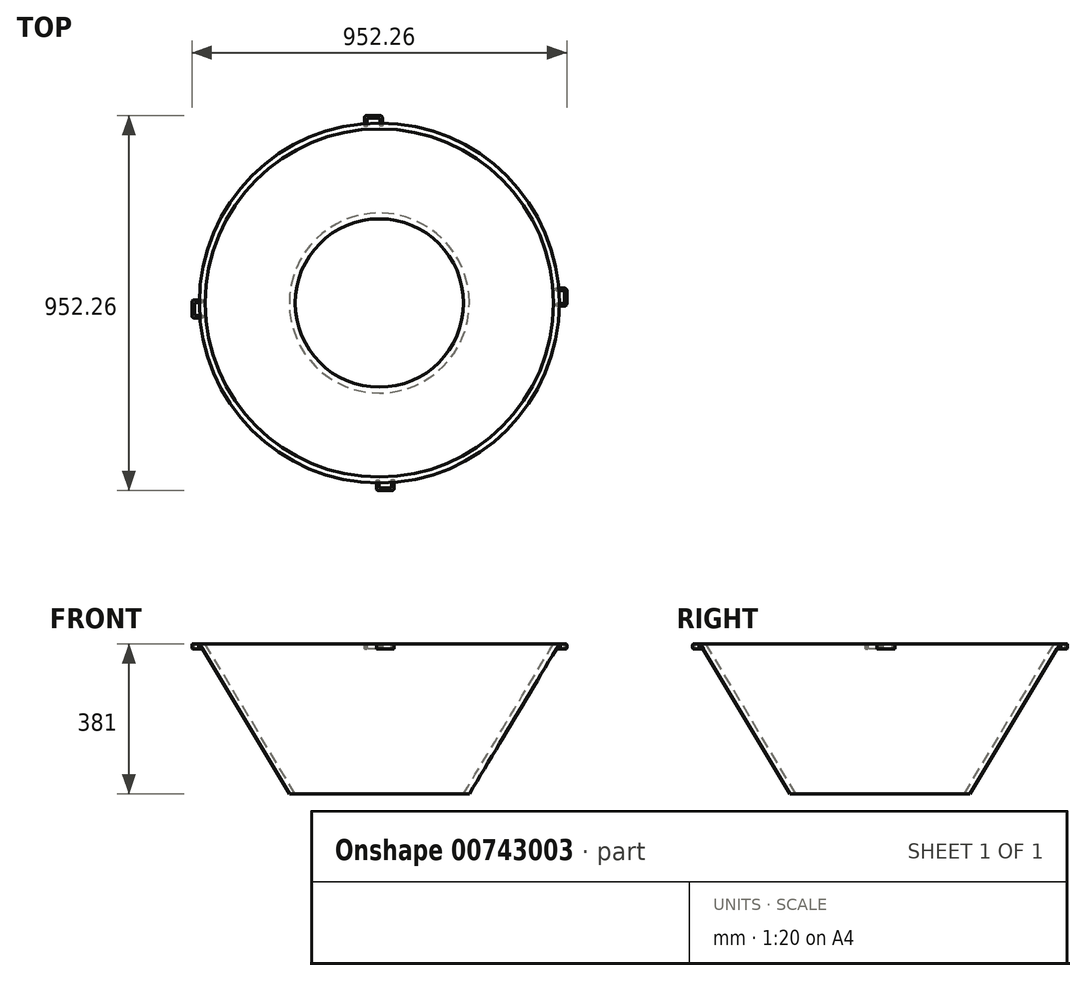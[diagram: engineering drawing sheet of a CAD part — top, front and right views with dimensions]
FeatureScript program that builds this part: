
annotation { "Feature Type Name" : "Feature", "Feature Type Description" : "" }
export const myFeature = defineFeature(function(context is Context, id is Id, definition is map)
    precondition{}
    {
        {
            var Q0;
            Q0=qCreatedBy(makeId("Top.planeOp"),FACE);
            var sketch = newSketch(context, id + "F0", { "sketchPlane" : qUnion([Q0])});
            skCircle(sketch, "E0", {"center": v(0, 0) * mm, "radius": 228.6 * mm});
            skSolve(sketch);
        }
        {
            var Q0;
            Q0=makeQuery(id+"F0.imprint","IMPRINT",FACE,{"disambiguationData":[TD([[makeQuery(id+"F0.imprint","IMPRINT",EDGE,{"derivedFrom":sQuery(id+"F0.wireOp",EDGE,"E0")}),1.0]])]});
            cPlane(context, id + "F1", {"entities" : qUnion([Q0]), "cplaneType" : CPlaneType.OFFSET, "offset" : 381 * mm, "width" : 152.4 * mm, "height" : 152.4 * mm});
        }
        {
            var Q0;
            Q0=qCreatedBy(id+"F1.planeOp",FACE);
            var sketch = newSketch(context, id + "F2", { "sketchPlane" : qUnion([Q0])});
            skCircle(sketch, "E1", {"center": v(0, 0) * mm, "radius": 457.2 * mm});
            skSolve(sketch);
        }
        {
            var Q0;
            Q0=makeQuery(id+"F0.imprint","IMPRINT",FACE,{"disambiguationData":[TD([[makeQuery(id+"F0.imprint","IMPRINT",EDGE,{"derivedFrom":sQuery(id+"F0.wireOp",EDGE,"E0")}),1.0]])]});
            var Q1;
            Q1=makeQuery(id+"F2.imprint","IMPRINT",FACE,{"disambiguationData":[TD([[makeQuery(id+"F2.imprint","IMPRINT",EDGE,{"derivedFrom":sQuery(id+"F2.wireOp",EDGE,"E1")}),1.0]])]});
            loft(context, id + "F3", {"sheetProfilesArray" : [{ "sheetProfileEntities" : qUnion([Q0]) }, { "sheetProfileEntities" : qUnion([Q1]) }]});
        }
        {
            var Q0;
            Q0=makeQuery(id+"F3.opLoft","CAP_FACE",FACE,{"disambiguationData":[OSD([makeQuery(id+"F2.imprint","IMPRINT",FACE,{"disambiguationData":[TD([[makeQuery(id+"F2.imprint","IMPRINT",EDGE,{"derivedFrom":sQuery(id+"F2.wireOp",EDGE,"E1")}),1.0]])]})])],"isStart":true});
            var Q1;
            Q1=makeQuery(id+"F3.opLoft","CAP_FACE",FACE,{"disambiguationData":[OSD([makeQuery(id+"F0.imprint","IMPRINT",FACE,{"disambiguationData":[TD([[makeQuery(id+"F0.imprint","IMPRINT",EDGE,{"derivedFrom":sQuery(id+"F0.wireOp",EDGE,"E0")}),1.0]])]})])],"isStart":true});
            shell(context, id + "F4", {"entities" : qUnion([Q0, Q1]), "thickness" : 12.7 * mm});
        }
        {
            var Q0;
            Q0=makeQuery(id+"F3.opLoft","CAP_FACE",FACE,{"disambiguationData":[OSD([makeQuery(id+"F2.imprint","IMPRINT",FACE,{"disambiguationData":[TD([[makeQuery(id+"F2.imprint","IMPRINT",EDGE,{"derivedFrom":sQuery(id+"F2.wireOp",EDGE,"E1")}),1.0]])]})])],"isStart":true});
            var sketch = newSketch(context, id + "F5", { "sketchPlane" : qUnion([Q0])});
            skLineSegment(sketch, "E2", {"start": v(-459.82, 1.27) * mm, "end": v(-469.78, 1.27) * mm});
            skLineSegment(sketch, "E3", {"start": v(-469.78, 1.27) * mm, "end": v(-469.78, -31.3) * mm});
            skLineSegment(sketch, "E4", {"start": v(-469.78, -31.3) * mm, "end": v(-459.82, -31.3) * mm});
            skLineSegment(sketch, "E5.0", {"start": v(-476.13, -37.65) * mm, "end": v(-459.82, -37.65) * mm});
            skLineSegment(sketch, "E5.1", {"start": v(-476.13, 7.62) * mm, "end": v(-476.13, -37.65) * mm});
            skLineSegment(sketch, "E5.2", {"start": v(-459.82, 7.62) * mm, "end": v(-476.13, 7.62) * mm});
            skLineSegment(sketch, "E6", {"start": v(-459.82, 7.62) * mm, "end": v(-459.82, 1.27) * mm});
            skLineSegment(sketch, "E7", {"start": v(-459.82, -31.3) * mm, "end": v(-459.82, -37.65) * mm});
            skSolve(sketch);
        }
        {
            var Q0;
            Q0=makeQuery(id+"F5.imprint","IMPRINT",FACE,{"disambiguationData":[TD([[makeQuery(id+"F5.imprint","IMPRINT",EDGE,{"derivedFrom":sQuery(id+"F5.wireOp",EDGE,"E2")}),-1.0]])]});
            extrude(context, id + "F6", {"entities" : qUnion([Q0]), "oppositeDirection" : true, "depth" : 12.7 * mm, "offsetDistance" : 25.4 * mm});
        }
        {
            var Q0;
            Q0=makeQuery(id+"F6.opExtrude","SWEPT_FACE",FACE,{"disambiguationData":[OSD([sQuery(id+"F5.wireOp",EDGE,"E6")])]});
            var sketch = newSketch(context, id + "F7", { "sketchPlane" : qUnion([Q0])});
            skLineSegment(sketch, "E8.0.0", {"start": v(7.62, 381) * mm, "end": v(1.27, 381) * mm});
            skLineSegment(sketch, "E8.0.1", {"start": v(1.27, 381) * mm, "end": v(1.27, 368.3) * mm});
            skLineSegment(sketch, "E8.0.2", {"start": v(1.27, 368.3) * mm, "end": v(7.62, 368.3) * mm});
            skLineSegment(sketch, "E8.0.3", {"start": v(7.62, 368.3) * mm, "end": v(7.62, 381) * mm});
            skLineSegment(sketch, "E9.0.0", {"start": v(-31.3, 381) * mm, "end": v(-37.65, 381) * mm});
            skLineSegment(sketch, "E9.0.1", {"start": v(-37.65, 381) * mm, "end": v(-37.65, 368.3) * mm});
            skLineSegment(sketch, "E9.0.2", {"start": v(-37.65, 368.3) * mm, "end": v(-31.3, 368.3) * mm});
            skLineSegment(sketch, "E9.0.3", {"start": v(-31.3, 368.3) * mm, "end": v(-31.3, 381) * mm});
            skSolve(sketch);
        }
        {
            var Q0;
            Q0=makeQuery(id+"F7.imprint","IMPRINT",FACE,{"disambiguationData":[TD([[makeQuery(id+"F7.imprint","IMPRINT",EDGE,{"derivedFrom":sQuery(id+"F7.wireOp",EDGE,"E8.0.0")}),1.0]])]});
            var Q1;
            Q1=makeQuery(id+"F7.imprint","IMPRINT",FACE,{"disambiguationData":[TD([[makeQuery(id+"F7.imprint","IMPRINT",EDGE,{"derivedFrom":sQuery(id+"F7.wireOp",EDGE,"E9.0.0")}),1.0]])]});
            extrude(context, id + "F8", {"entities" : qUnion([Q0, Q1]), "endBound" : BoundingType.UP_TO_NEXT, "depth" : 25.4 * mm, "offsetDistance" : 25.4 * mm});
        }
        {
            var Q0;
            Q0=makeQuery(id+"F6.opExtrude","SWEPT_EDGE",EDGE,{"disambiguationData":[OSD([sQuery(id+"F5.wireOp",EDGE,"E5.0"),sQuery(id+"F5.wireOp",EDGE,"E5.1")])]});
            var Q1;
            Q1=makeQuery(id+"F6.opExtrude","SWEPT_EDGE",EDGE,{"disambiguationData":[OSD([sQuery(id+"F5.wireOp",EDGE,"E5.1"),sQuery(id+"F5.wireOp",EDGE,"E5.2")])]});
            fillet(context, id + "F9", {"entities" : qUnion([Q0, Q1]), "radius" : 5.08 * mm, "tangentPropagation" : true, "allowEdgeOverflow" : false});
        }
        {
            var Q0;
            Q0=makeQuery(id+"F6.opExtrude","CAP_EDGE",EDGE,{"disambiguationData":[OSD([sQuery(id+"F5.wireOp",EDGE,"E5.1")])],"isStart":true});
            var Q1;
            Q1=makeQuery(id+"F6.opExtrude","CAP_EDGE",EDGE,{"disambiguationData":[OSD([sQuery(id+"F5.wireOp",EDGE,"E5.1")])],"isStart":false});
            fillet(context, id + "F10", {"entities" : qUnion([Q0, Q1]), "radius" : 2.54 * mm, "tangentPropagation" : true, "allowEdgeOverflow" : false});
        }
        {
            var Q0;
            Q0=makeQuery(id+"F6.opExtrude","SWEPT_BODY",BODY,{"disambiguationData":[OSD([sQuery(id+"F5.wireOp",EDGE,"E2"),sQuery(id+"F5.wireOp",EDGE,"E3"),sQuery(id+"F5.wireOp",EDGE,"E4"),sQuery(id+"F5.wireOp",EDGE,"E5.0"),sQuery(id+"F5.wireOp",EDGE,"E5.1"),sQuery(id+"F5.wireOp",EDGE,"E5.2"),sQuery(id+"F5.wireOp",EDGE,"E6"),sQuery(id+"F5.wireOp",EDGE,"E7")])]});
            var Q1;
            Q1=makeQuery(id+"F8.opExtrude","SWEPT_BODY",BODY,{"disambiguationData":[OSD([sQuery(id+"F7.wireOp",EDGE,"E9.0.0"),sQuery(id+"F7.wireOp",EDGE,"E9.0.1"),sQuery(id+"F7.wireOp",EDGE,"E9.0.2"),sQuery(id+"F7.wireOp",EDGE,"E9.0.3")])]});
            var Q2;
            Q2=makeQuery(id+"F8.opExtrude","SWEPT_BODY",BODY,{"disambiguationData":[OSD([sQuery(id+"F7.wireOp",EDGE,"E8.0.0"),sQuery(id+"F7.wireOp",EDGE,"E8.0.1"),sQuery(id+"F7.wireOp",EDGE,"E8.0.2"),sQuery(id+"F7.wireOp",EDGE,"E8.0.3")])]});
            var Q3;
            Q3=makeQuery(id+"F4.opShell","OFFSET_FACE",FACE,{"disambiguationData":[OSD([sQuery(id+"F0.wireOp",EDGE,"E0"),sQuery(id+"F2.wireOp",EDGE,"E1")])]});
            circularPattern(context, id + "F11", {"entities" : qUnion([Q0, Q1, Q2]), "axis" : qUnion([Q3]), "angle" : 360 * degree, "instanceCount" : 4, "equalSpace" : true});
        }
    });
